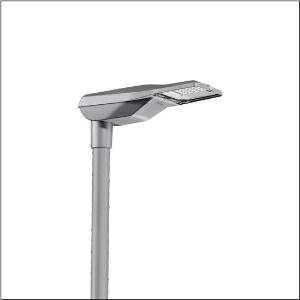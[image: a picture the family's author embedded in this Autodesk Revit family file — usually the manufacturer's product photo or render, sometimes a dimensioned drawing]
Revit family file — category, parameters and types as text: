
# Revit family: streetlight_sl_21_iq_micro___st1_0a_5xe1d61d08cb_4c5c
name_source: partatom
category: Lighting Fixtures
units: mm (PartAtom-declared; Revit-internal decimal feet)

## family parameters
Cut with Voids When Loaded = No
Host = Face
Light Source = No
Part Type = Normal
Room Calculation Point = No
Round Connector Dimension = Use Diameter
Shared = No

## types (1)
- --- (1 x LED, 2570 lm, 19.4 W, 2700K)
    Apparent Load = 19 VA
    CIE Flux Codes = 37 72 97 100 100
    Color Rendering = 70
    Color Temperature = 2700K
    Default Elevation = 1800 mm
    Description = Streetlight SL 21 iQ micro, mast luminaire, primary light control with lens, of PMMA, primary optical cover: cover, of toughened safety glass, transparent, light distribution: ST1.0a, light emission: direct distribution, primary light characteristic: asymmetric, installation type: post-top, side-entry, LED, High Power LED, rated luminous flux: 2.570lm, luminous efficacy: 133lm/W, light colour: 727, colour temperature: 2700K, control: Auto-Match, Temp-Guard, Lumen-Switch, Night-Set, Smart-Wire, Light-Fading, Desk-Remote (wireless, voltage-free reading and setting of iQ features in the workshop via application-optimized NFC function/RFID function), optimised constant luminous flux control (CLO 2.0), presetting dimming linear, mains connection: 220..240V, AC, 50/60Hz, start of lifetime: 19W, end of service life: 20W, reduction: 10W, luminaire housing, of diecast aluminium, powder-coated, Siteco® metallic grey (DB 702S), corrosivity category C5 mid according to DIN EN ISO 12944, please order mast flange separately, inclination adjustable: 0°, 5°, 10°, 15°, sealing non-destructively replaceable, multi-level sealing system, length: 528mm, width: 235mm, height: 110mm, mast flange for spigot size: 42mm (side-entry): 5XC10008XM4, 60/48mm (side-entry/post-top): 5XC10108XM2, 76/60mm (side-entry/post-top): 5XC10108XM1, protection rating (complete): IP66, insulation class (complete): insulation class II (safety insulation), certification: CE, ENEC, ENEC+, VDE, impact resistance: IK09, permissible operating ambient temperature for outdoor applications: -40..+50°C, standard-compliant lighting for roads and squares, packaging unit: 1 piece

Light Distribution: ST1.0a
    Height = 110 mm
    Lamp = 1 x LED
    Lamp Light Flux = 2570 lm
    Lamp Power = 19.4 W
    Lamp count = 1
    Length = 528 mm
    Luminous efficacy = 132 lm/W
    Manufacturer = Siteco
    ModVariant = No
    Model = 5XE1D61D08CB
    Number of Poles = 1
    OnlyDefault = Yes
    Power Factor = 1
    Product Name = Streetlight SL 21 iQ micro | ST1.0a
    Product group = mast luminaire | pylon top
    ProductGroupID = 6100
    Protection Class = Protection class II
    Protection Degree = IP 66
    RLX_Detail_Level = 1
    RLX_Emergency_Light_Flux = 0 lm
    RLX_Emergency_Type = 0
    RLX_Emergency_Type_DB = No
    RlxData = <blob elided: 98737 chars, md5=029c44de>
    Socket = socket
    Standby Power = 0 W
    System Light Flux = 2570 lm
    System Power = 19 W
    Type Comments = factory setting: luminous flux: 100 % | dim-lin: 254 | 387 mA
    Type Image = l_1006881.jpg
    URL = http://relux.com
    VarID = @adj_070469
    Voltage = 0 V
    Weight = 0.00 kg
    Width = 235 mm

## geometry (parser evidence)
native form markers: Blend x4, Sweep x12
no freeform markers — native parametric forms only
